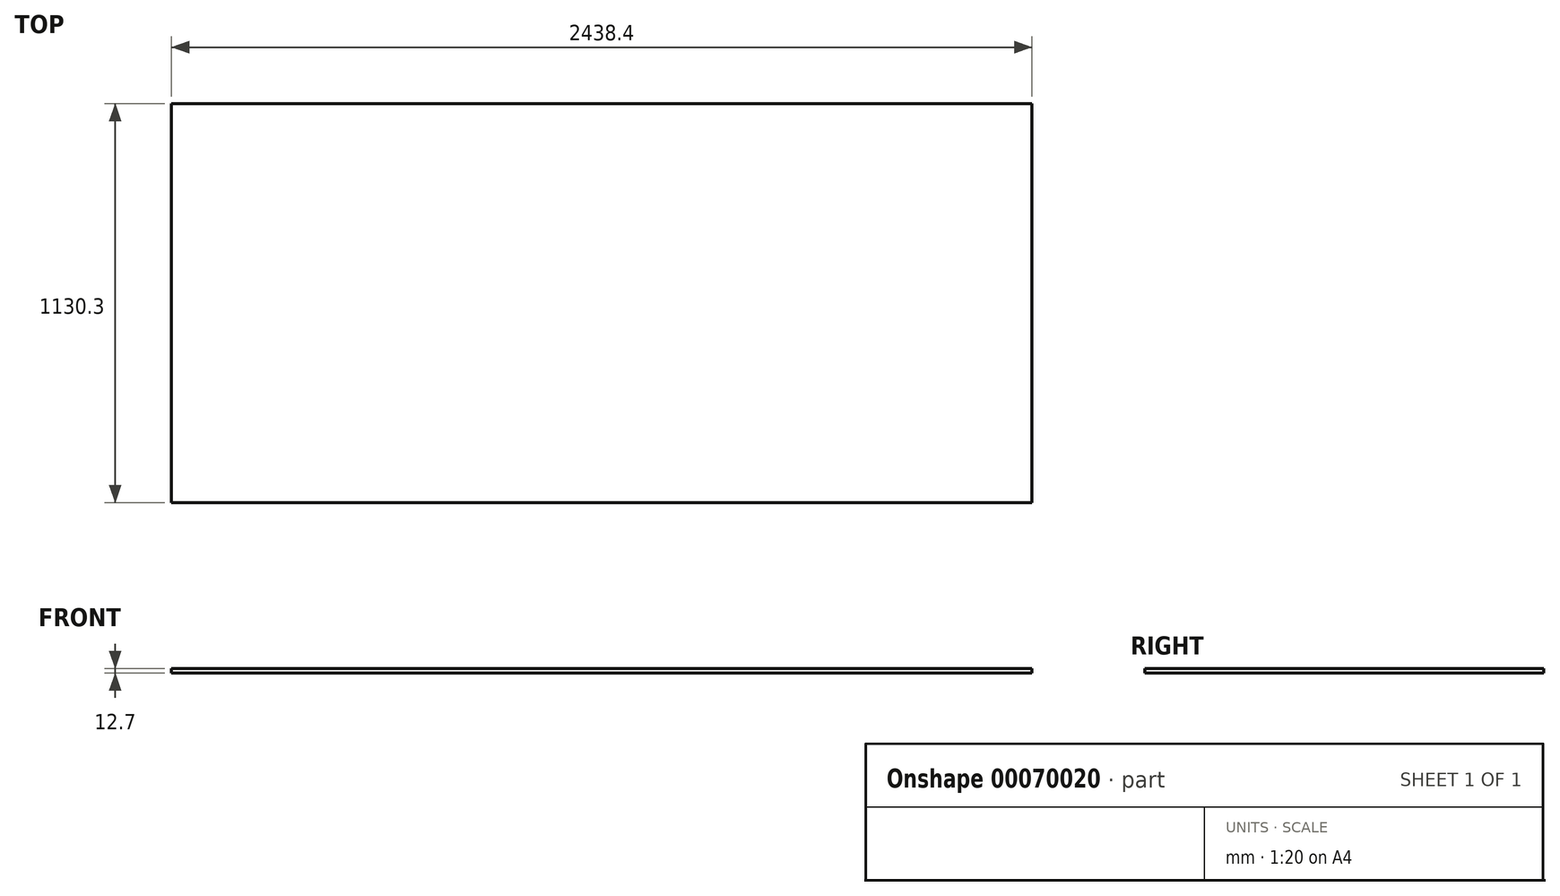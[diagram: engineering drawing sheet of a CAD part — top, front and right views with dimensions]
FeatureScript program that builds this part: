
annotation { "Feature Type Name" : "Feature", "Feature Type Description" : "" }
export const myFeature = defineFeature(function(context is Context, id is Id, definition is map)
    precondition{}
    {
        {
            var Q0;
            Q0=qCreatedBy(makeId("Top.planeOp"),FACE);
            var sketch = newSketch(context, id + "F0", { "sketchPlane" : qUnion([Q0])});
            skLineSegment(sketch, "E0.bottom", {"start": v(2.57, 0) * mm, "end": v(2440.97, 0) * mm});
            skLineSegment(sketch, "E0.top", {"start": v(2.57, 1130.3) * mm, "end": v(2440.97, 1130.3) * mm});
            skLineSegment(sketch, "E0.left", {"start": v(2.57, 0) * mm, "end": v(2.57, 1130.3) * mm});
            skLineSegment(sketch, "E0.right", {"start": v(2440.97, 0) * mm, "end": v(2440.97, 1130.3) * mm});
            skSolve(sketch);
        }
        {
            var Q0;
            Q0=makeQuery(id+"F0.imprint","IMPRINT",FACE,{"disambiguationData":[TD([[makeQuery(id+"F0.imprint","IMPRINT",EDGE,{"derivedFrom":sQuery(id+"F0.wireOp",EDGE,"E0.bottom")}),1.0]])]});
            extrude(context, id + "F1", {"entities" : qUnion([Q0]), "depth" : 12.7 * mm});
        }
    });
